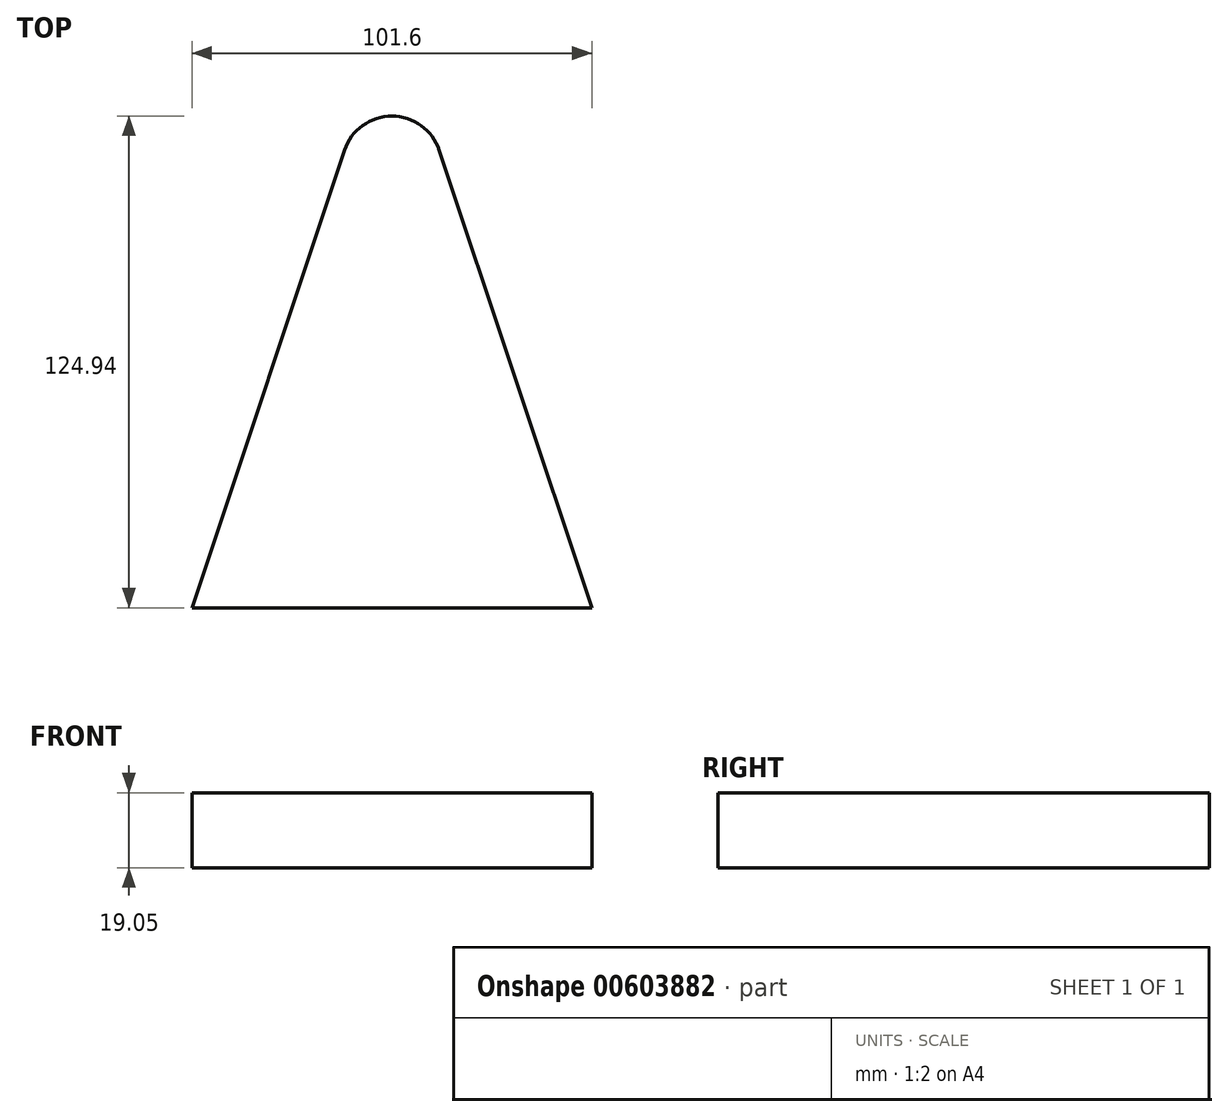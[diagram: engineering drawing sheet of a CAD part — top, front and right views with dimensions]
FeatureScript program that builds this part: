
annotation { "Feature Type Name" : "Feature", "Feature Type Description" : "" }
export const myFeature = defineFeature(function(context is Context, id is Id, definition is map)
    precondition{}
    {
        {
            var Q0;
            Q0=qCreatedBy(makeId("Top.planeOp"),FACE);
            var sketch = newSketch(context, id + "F0", { "sketchPlane" : qUnion([Q0])});
            skLineSegment(sketch, "E0", {"start": v(0, 0) * mm, "end": v(-50.8, 0) * mm});
            skLineSegment(sketch, "E1", {"start": v(-50.8, 0) * mm, "end": v(0, 152.4) * mm});
            skLineSegment(sketch, "E2", {"start": v(0, 152.4) * mm, "end": v(50.8, 0) * mm});
            skLineSegment(sketch, "E3", {"start": v(50.8, 0) * mm, "end": v(0, 0) * mm});
            skSolve(sketch);
        }
        {
            var Q0;
            Q0=makeQuery(id+"F0.imprint","IMPRINT",FACE,{"disambiguationData":[TD([[makeQuery(id+"F0.imprint","IMPRINT",EDGE,{"derivedFrom":sQuery(id+"F0.wireOp",EDGE,"E0")}),-1.0]])]});
            extrude(context, id + "F1", {"entities" : qUnion([Q0]), "depth" : 19.05 * mm, "offsetDistance" : 25.4 * mm});
        }
        {
            var Q0;
            Q0=makeQuery(id+"F1.opExtrude","SWEPT_EDGE",EDGE,{"disambiguationData":[OSD([sQuery(id+"F0.wireOp",EDGE,"E1"),sQuery(id+"F0.wireOp",EDGE,"E2")])]});
            fillet(context, id + "F2", {"entities" : qUnion([Q0]), "radius" : 12.7 * mm, "tangentPropagation" : true, "allowEdgeOverflow" : false});
        }
    });
